# Revit family: MBS_bedside table
name_source: partatom
category: Generic Models
revit_build: Autodesk Revit 2014 (Build: 20130308_1515(x64)
units: mm (PartAtom-declared; Revit-internal decimal feet)

## types (2) — shared parameters
c_clos back pan height = 500 mm  [stored 1.64042 ft]
c_clos back pan widht = 560 mm  [stored 1.83727 ft]
c_clos bas pan depht = 350 mm  [stored 1.14829 ft]
c_clos bas pan widht = 500 mm  [stored 1.64042 ft]
c_clos side pan height = 500 mm  [stored 1.64042 ft]
c_clos side panel depht = 350 mm  [stored 1.14829 ft]
c_darw bott depht = 350 mm  [stored 1.14829 ft]
c_draw bott widht = 440 mm  [stored 1.44357 ft]
c_draw side height = 200 mm  [stored 0.656168 ft]
c_drawer front height = 230 mm  [stored 0.754593 ft]
c_drawer front widht = 560 mm  [stored 1.83727 ft]
c_drawer side widht = 350 mm  [stored 1.14829 ft]
c_top depht = 410 mm  [stored 1.34514 ft]
c_top widht = 560 mm  [stored 1.83727 ft]
panel thickness = 30 mm  [stored 0.0984252 ft]
top thickness = 50 mm  [stored 0.164042 ft]

## per-type parameters (varying)
| type | closet material |
| bedside table main room | Polyvinyl Chloride, Rigid BEDSIDE2 MBS |
| bedside table second room | Polyvinyl Chloride, Rigid BEDSIDE TABLE1 MBS |

note: [stored X ft] marks values corroborated as IEEE doubles in the binary element streams (Revit-internal decimal feet)

## geometry (parser evidence)
native form markers: Sweep x1
no freeform markers — native parametric forms only
